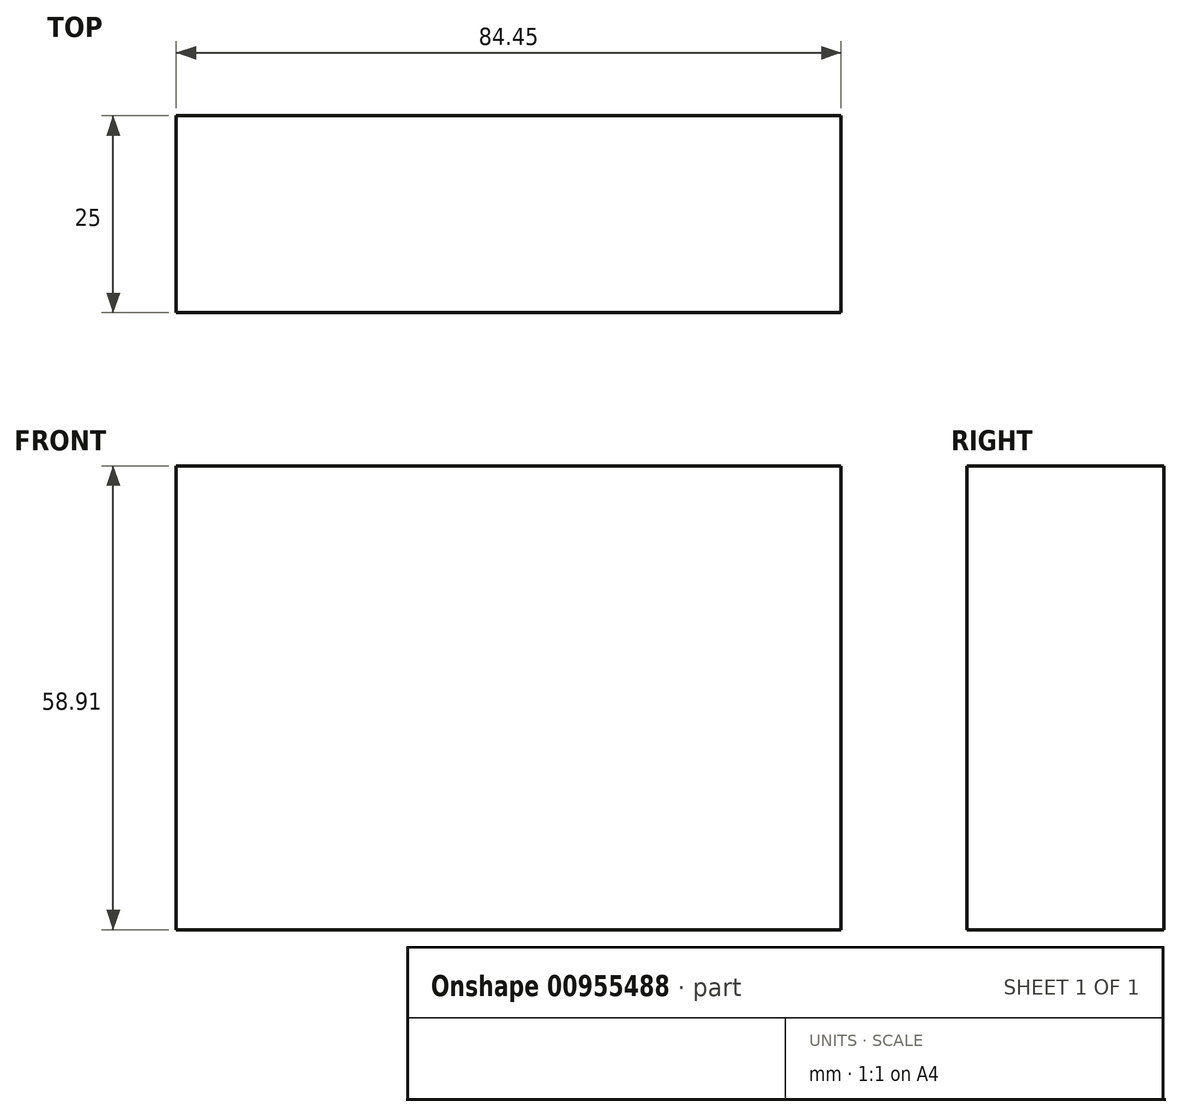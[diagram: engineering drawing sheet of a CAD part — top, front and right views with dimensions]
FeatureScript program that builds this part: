
annotation { "Feature Type Name" : "Feature", "Feature Type Description" : "" }
export const myFeature = defineFeature(function(context is Context, id is Id, definition is map)
    precondition{}
    {
        {
            var Q0;
            Q0=qCreatedBy(makeId("Front.planeOp"),FACE);
            var sketch = newSketch(context, id + "F0", { "sketchPlane" : qUnion([Q0])});
            skLineSegment(sketch, "E0.bottom", {"start": v(-74.37, 31.57) * mm, "end": v(10.08, 31.57) * mm});
            skLineSegment(sketch, "E0.top", {"start": v(-74.37, -27.34) * mm, "end": v(10.08, -27.34) * mm});
            skLineSegment(sketch, "E0.left", {"start": v(-74.37, 31.57) * mm, "end": v(-74.37, -27.34) * mm});
            skLineSegment(sketch, "E0.right", {"start": v(10.08, 31.57) * mm, "end": v(10.08, -27.34) * mm});
            skSolve(sketch);
        }
        {
            var Q0;
            Q0 = qSketchRegion(id + "F0", true);
            extrude(context, id + "F1", {"entities" : qUnion([Q0]), "depth" : 25 * mm, "offsetDistance" : 25 * mm});
        }
    });
